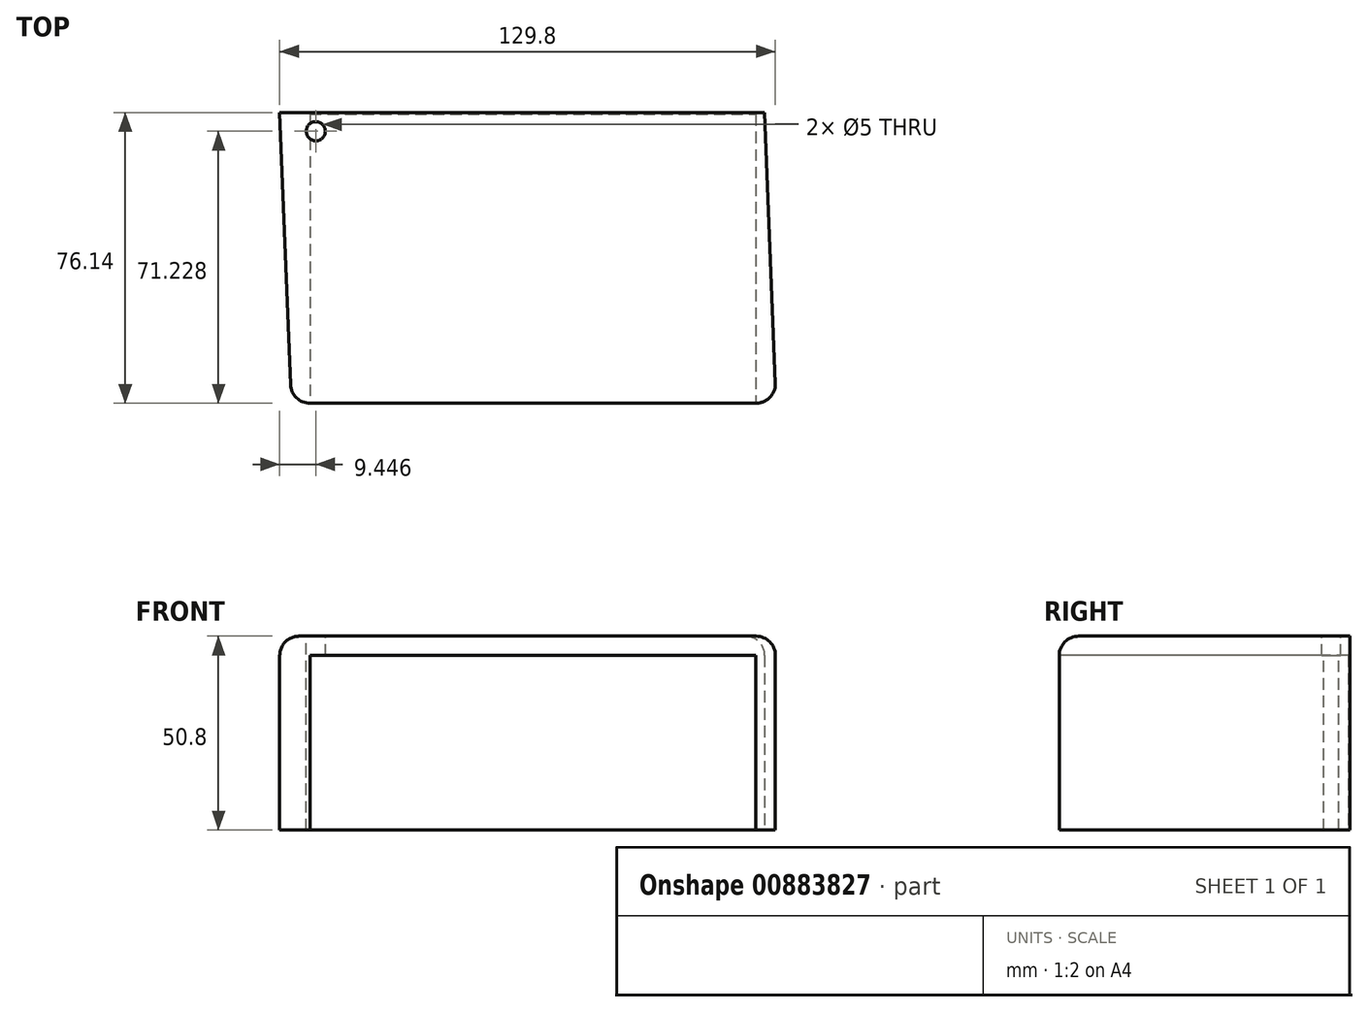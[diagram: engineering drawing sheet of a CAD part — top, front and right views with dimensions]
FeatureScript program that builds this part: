
annotation { "Feature Type Name" : "Feature", "Feature Type Description" : "" }
export const myFeature = defineFeature(function(context is Context, id is Id, definition is map)
    precondition{}
    {
        {
            var Q0;
            Q0=qCreatedBy(makeId("Top.planeOp"),FACE);
            var sketch = newSketch(context, id + "F0", { "sketchPlane" : qUnion([Q0])});
            skLineSegment(sketch, "E0", {"start": v(0, 0) * mm, "end": v(127, 0) * mm});
            skLineSegment(sketch, "E1", {"start": v(127, 0) * mm, "end": v(124, 76.14) * mm});
            skLineSegment(sketch, "E2", {"start": v(124, 76.14) * mm, "end": v(-3, 76.14) * mm});
            skLineSegment(sketch, "E3", {"start": v(-3, 76.14) * mm, "end": v(0, 0) * mm});
            skSolve(sketch);
        }
        {
            var Q0;
            Q0 = qSketchRegion(id + "F0", true);
            extrude(context, id + "F1", {"entities" : qUnion([Q0]), "depth" : 50.8 * mm, "offsetDistance" : 25.4 * mm});
        }
        {
            var Q0;
            Q0=makeQuery(id+"F1.opExtrude","CAP_EDGE",EDGE,{"disambiguationData":[OSD([sQuery(id+"F0.wireOp",EDGE,"E0")])],"isStart":false});
            var Q1;
            Q1=makeQuery(id+"F1.opExtrude","CAP_EDGE",EDGE,{"disambiguationData":[OSD([sQuery(id+"F0.wireOp",EDGE,"E1")])],"isStart":false});
            var Q2;
            Q2=makeQuery(id+"F1.opExtrude","SWEPT_EDGE",EDGE,{"disambiguationData":[OSD([sQuery(id+"F0.wireOp",EDGE,"E0"),sQuery(id+"F0.wireOp",EDGE,"E1")])]});
            var Q3;
            Q3=makeQuery(id+"F1.opExtrude","SWEPT_EDGE",EDGE,{"disambiguationData":[OSD([sQuery(id+"F0.wireOp",EDGE,"E0"),sQuery(id+"F0.wireOp",EDGE,"E3")])]});
            var Q4;
            Q4=makeQuery(id+"F1.opExtrude","CAP_EDGE",EDGE,{"disambiguationData":[OSD([sQuery(id+"F0.wireOp",EDGE,"E3")])],"isStart":false});
            fillet(context, id + "F2", {"entities" : qUnion([Q0, Q1, Q2, Q3, Q4]), "radius" : 5.08 * mm, "tangentPropagation" : true, "allowEdgeOverflow" : false});
        }
        {
            var Q0;
            Q0=makeQuery(id+"F1.opExtrude","SWEPT_FACE",FACE,{"disambiguationData":[OSD([sQuery(id+"F0.wireOp",EDGE,"E0")])]});
            extrude(context, id + "F3", {"entities" : qUnion([Q0]), "operationType" : NewBodyOperationType.REMOVE, "oppositeDirection" : true, "depth" : 75.7 * mm, "offsetDistance" : 25.4 * mm});
        }
        {
            var Q0;
            Q0=makeQuery(id+"F1.opExtrude","CAP_FACE",FACE,{"disambiguationData":[OSD([sQuery(id+"F0.wireOp",EDGE,"E0"),sQuery(id+"F0.wireOp",EDGE,"E1"),sQuery(id+"F0.wireOp",EDGE,"E2"),sQuery(id+"F0.wireOp",EDGE,"E3")])],"isStart":false});
            var sketch = newSketch(context, id + "F4", { "sketchPlane" : qUnion([Q0])});
            skPoint(sketch, "E4", {"position": v(6.45, 71.23) * mm});
            skSolve(sketch);
        }
        {
            var Q0;
            Q0=sQuery(id+"F4.wireOp",VERTEX,"E4");
            var Q1;
            Q1=makeQuery(id+"F1.opExtrude","SWEPT_BODY",BODY,{"disambiguationData":[OSD([sQuery(id+"F0.wireOp",EDGE,"E0"),sQuery(id+"F0.wireOp",EDGE,"E1"),sQuery(id+"F0.wireOp",EDGE,"E2"),sQuery(id+"F0.wireOp",EDGE,"E3")])]});
            hole(context, id + "F5", {"style" : HoleStyle.SIMPLE, "endStyle" : HoleEndStyle.THROUGH, "holeDiameter" : 5 * mm, "majorDiameter" : 5 * mm, "isTappedThrough" : true, "tappedDepth" : 12 * mm, "tapClearance" : 3, "locations" : qUnion([Q0]), "scope" : qUnion([Q1])});
        }
    });
